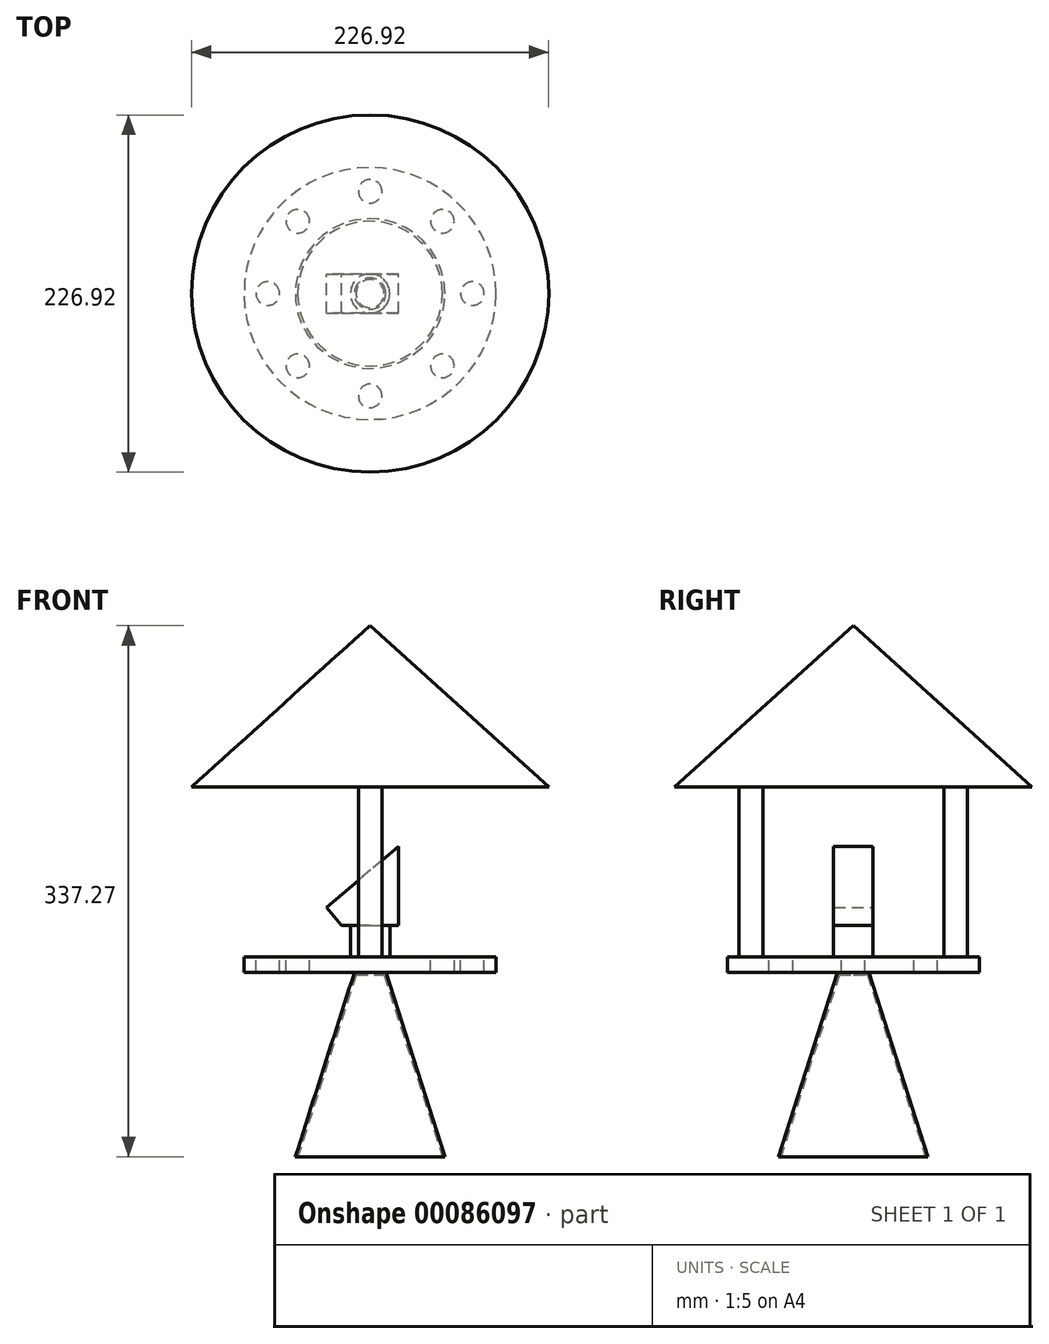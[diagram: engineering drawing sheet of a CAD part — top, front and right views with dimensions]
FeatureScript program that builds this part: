
annotation { "Feature Type Name" : "Feature", "Feature Type Description" : "" }
export const myFeature = defineFeature(function(context is Context, id is Id, definition is map)
    precondition{}
    {
        {
            var Q0;
            Q0=qCreatedBy(makeId("Front.planeOp"),FACE);
            var sketch = newSketch(context, id + "F0", { "sketchPlane" : qUnion([Q0])});
            skLineSegment(sketch, "E0", {"start": v(0, 58.5) * mm, "end": v(10, 58.5) * mm});
            skLineSegment(sketch, "E1", {"start": v(10, 58.5) * mm, "end": v(47.5, -58.5) * mm});
            skLineSegment(sketch, "E2", {"start": v(47.5, -58.5) * mm, "end": v(0, -58.5) * mm});
            skLineSegment(sketch, "E3", {"start": v(0, -58.5) * mm, "end": v(0, 58.5) * mm});
            skPoint(sketch, "E4", {"position": v(0, 0) * mm});
            skSolve(sketch);
        }
        {
            var Q0;
            Q0 = qSketchRegion(id + "F0", true);
            var Q1;
            Q1=sQuery(id+"F0.wireOp",EDGE,"E3");
            revolve(context, id + "F1", {"entities" : qUnion([Q0]), "axis" : qUnion([Q1]), "revolveType" : RevolveType.FULL});
        }
        {
            var Q0;
            Q0=makeQuery(id+"F1.opRevolve","SWEPT_FACE",FACE,{"disambiguationData":[OSD([sQuery(id+"F0.wireOp",EDGE,"E2")])]});
            shell(context, id + "F2", {"entities" : qUnion([Q0]), "thickness" : 1.5 * mm});
        }
        {
            var Q0;
            Q0=makeQuery(id+"F1.opRevolve","SWEPT_FACE",FACE,{"disambiguationData":[OSD([sQuery(id+"F0.wireOp",EDGE,"E0")])]});
            var sketch = newSketch(context, id + "F3", { "sketchPlane" : qUnion([Q0])});
            skCircle(sketch, "E5", {"center": v(0, 0) * mm, "radius": 80 * mm});
            skSolve(sketch);
        }
        {
            var Q0;
            Q0 = qSketchRegion(id + "F3", true);
            extrude(context, id + "F4", {"entities" : qUnion([Q0]), "operationType" : NewBodyOperationType.ADD, "depth" : 10 * mm});
        }
        {
            var Q0;
            Q0=makeQuery(id+"F4.opExtrude","CAP_FACE",FACE,{"disambiguationData":[OSD([sQuery(id+"F3.wireOp",EDGE,"E5")])],"isStart":false});
            var sketch = newSketch(context, id + "F5", { "sketchPlane" : qUnion([Q0])});
            skCircle(sketch, "E6", {"center": v(-65, 0) * mm, "radius": 7.5 * mm});
            skCircle(sketch, "E7.1.0", {"center": v(-45.96, -45.96) * mm, "radius": 7.5 * mm});
            skCircle(sketch, "E7.2.0", {"center": v(0, -65) * mm, "radius": 7.5 * mm});
            skCircle(sketch, "E7.3.0", {"center": v(45.96, -45.96) * mm, "radius": 7.5 * mm});
            skCircle(sketch, "E7.4.0", {"center": v(65, 0) * mm, "radius": 7.5 * mm});
            skCircle(sketch, "E7.5.0", {"center": v(45.96, 45.96) * mm, "radius": 7.5 * mm});
            skCircle(sketch, "E7.6.0", {"center": v(0, 65) * mm, "radius": 7.5 * mm});
            skCircle(sketch, "E7.7.0", {"center": v(-45.96, 45.96) * mm, "radius": 7.5 * mm});
            skPoint(sketch, "E7.center", {"position": v(0, 0) * mm});
            skSolve(sketch);
        }
        {
            var Q0;
            Q0 = qSketchRegion(id + "F5", true);
            extrude(context, id + "F6", {"entities" : qUnion([Q0]), "operationType" : NewBodyOperationType.REMOVE, "endBound" : BoundingType.UP_TO_NEXT, "oppositeDirection" : true, "depth" : 25 * mm});
        }
        {
            var Q0;
            Q0=makeQuery(id+"F4.opExtrude","CAP_FACE",FACE,{"disambiguationData":[OSD([sQuery(id+"F3.wireOp",EDGE,"E5")])],"isStart":false});
            var sketch = newSketch(context, id + "F7", { "sketchPlane" : qUnion([Q0])});
            skCircle(sketch, "E8", {"center": v(0, 0) * mm, "radius": 12.5 * mm});
            skSolve(sketch);
        }
        {
            var Q0;
            Q0 = qSketchRegion(id + "F7", true);
            extrude(context, id + "F8", {"entities" : qUnion([Q0]), "operationType" : NewBodyOperationType.ADD, "depth" : 20 * mm});
        }
        {
            var Q0;
            Q0=qCreatedBy(makeId("Front.planeOp"),FACE);
            var sketch = newSketch(context, id + "F9", { "sketchPlane" : qUnion([Q0])});
            skLineSegment(sketch, "E9", {"start": v(-18, 88.5) * mm, "end": v(18, 88.5) * mm});
            skPoint(sketch, "E10", {"position": v(0, 88.5) * mm});
            skLineSegment(sketch, "E11", {"start": v(18, 88.5) * mm, "end": v(18, 138.5) * mm});
            skLineSegment(sketch, "E12", {"start": v(18, 138.5) * mm, "end": v(-27.67, 99.96) * mm});
            skLineSegment(sketch, "E13", {"start": v(-27.67, 99.96) * mm, "end": v(-18, 88.5) * mm});
            skSolve(sketch);
        }
        {
            var Q0;
            Q0 = qSketchRegion(id + "F9", true);
            extrude(context, id + "F10", {"entities" : qUnion([Q0]), "operationType" : NewBodyOperationType.ADD, "endBound" : BoundingType.SYMMETRIC, "depth" : 25 * mm});
        }
        {
            var Q0;
            Q0=makeQuery(id+"F4.opExtrude","CAP_FACE",FACE,{"disambiguationData":[OSD([sQuery(id+"F3.wireOp",EDGE,"E5")])],"isStart":true});
            var sketch = newSketch(context, id + "F11", { "sketchPlane" : qUnion([Q0])});
            skCircle(sketch, "E14.0", {"center": v(0, -65) * mm, "radius": 7.5 * mm});
            skCircle(sketch, "E15.0", {"center": v(0, 65) * mm, "radius": 7.5 * mm});
            skSolve(sketch);
        }
        {
            var Q0;
            Q0 = qSketchRegion(id + "F11", true);
            extrude(context, id + "F12", {"entities" : qUnion([Q0]), "operationType" : NewBodyOperationType.ADD, "oppositeDirection" : true, "depth" : 150 * mm});
        }
        {
            var Q0;
            Q0=qCreatedBy(makeId("Right.planeOp"),FACE);
            var sketch = newSketch(context, id + "F13", { "sketchPlane" : qUnion([Q0])});
            skLineSegment(sketch, "E16", {"start": v(-113.46, 176.43) * mm, "end": v(0, 278.77) * mm});
            skLineSegment(sketch, "E17", {"start": v(0, 278.77) * mm, "end": v(0, 176.43) * mm});
            skLineSegment(sketch, "E18", {"start": v(0, 176.43) * mm, "end": v(-113.46, 176.43) * mm});
            skSolve(sketch);
        }
        {
            var Q0;
            Q0=makeQuery(id+"F13.imprint","IMPRINT",FACE,{"disambiguationData":[TD([[makeQuery(id+"F13.imprint","IMPRINT",EDGE,{"derivedFrom":sQuery(id+"F13.wireOp",EDGE,"E16")}),-1.0]])]});
            var Q1;
            Q1=sQuery(id+"F13.wireOp",EDGE,"E17");
            revolve(context, id + "F14", {"operationType" : NewBodyOperationType.ADD, "entities" : qUnion([Q0]), "axis" : qUnion([Q1]), "revolveType" : RevolveType.FULL});
        }
    });
